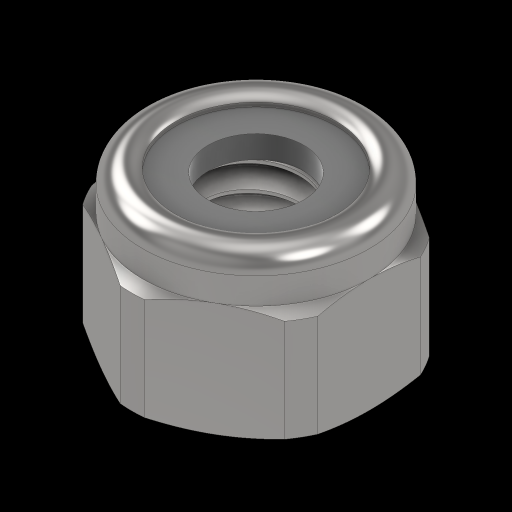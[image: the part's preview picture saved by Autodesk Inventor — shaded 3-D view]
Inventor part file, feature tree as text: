
AUTODESK INVENTOR PART (.ipt)
format: ipt  version: 2024.2 (Build 282272000, 272)  size: 393,216 bytes
history: native  units: in
note: dims shown in document units (in); Inventor stores cm internally (conversion verified against a paired STEP export)
features: revolve x1, boolean_combine x1
ambient origin geometry x8: Origin, YZ Plane, XZ Plane, XY Plane, X Axis, Y Axis, Z Axis, Center Point
bodies: Solid1 (feature_tree), Solid2 (feature_tree)
feature tree (2):
  revolve  "Revolve1"  [1 undecoded]
  boolean_combine  "Combine1"
note: 1 required parameter value undecoded (feature->parameter linkage not recoverable at this tier; creation-order binding heuristic only, values carry confidence <= 0.55)
